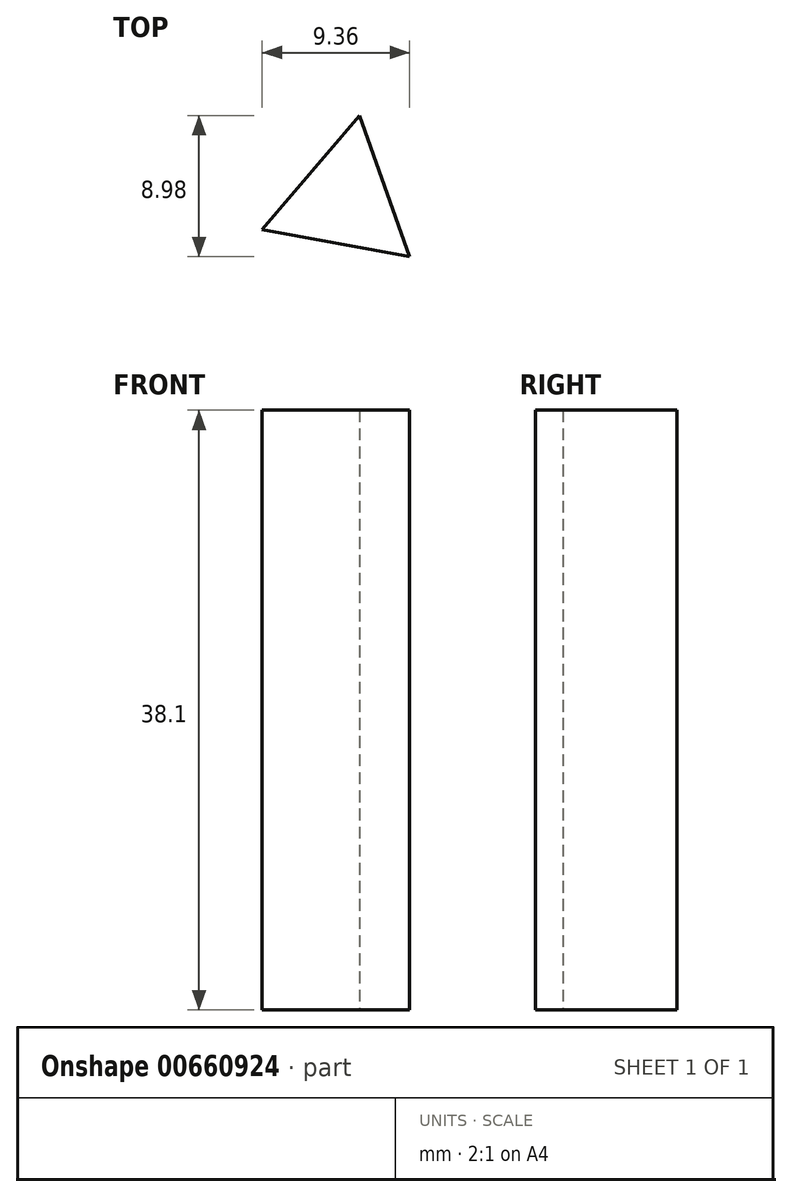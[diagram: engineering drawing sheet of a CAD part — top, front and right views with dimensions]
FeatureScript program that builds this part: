
annotation { "Feature Type Name" : "Feature", "Feature Type Description" : "" }
export const myFeature = defineFeature(function(context is Context, id is Id, definition is map)
    precondition{}
    {
        {
            var Q0;
            Q0=qCreatedBy(makeId("Top.planeOp"),FACE);
            var sketch = newSketch(context, id + "F0", { "sketchPlane" : qUnion([Q0])});
            skLineSegment(sketch, "E0", {"start": v(-50.51, 26.4) * mm, "end": v(-44.32, 33.64) * mm});
            skLineSegment(sketch, "E1", {"start": v(-44.32, 33.64) * mm, "end": v(-41.15, 24.66) * mm});
            skLineSegment(sketch, "E2", {"start": v(-41.15, 24.66) * mm, "end": v(-50.51, 26.4) * mm});
            skSolve(sketch);
        }
        {
            var Q0;
            Q0 = qSketchRegion(id + "F0", true);
            extrude(context, id + "F1", {"entities" : qUnion([Q0]), "depth" : 38.1 * mm, "offsetDistance" : 25.4 * mm});
        }
    });
